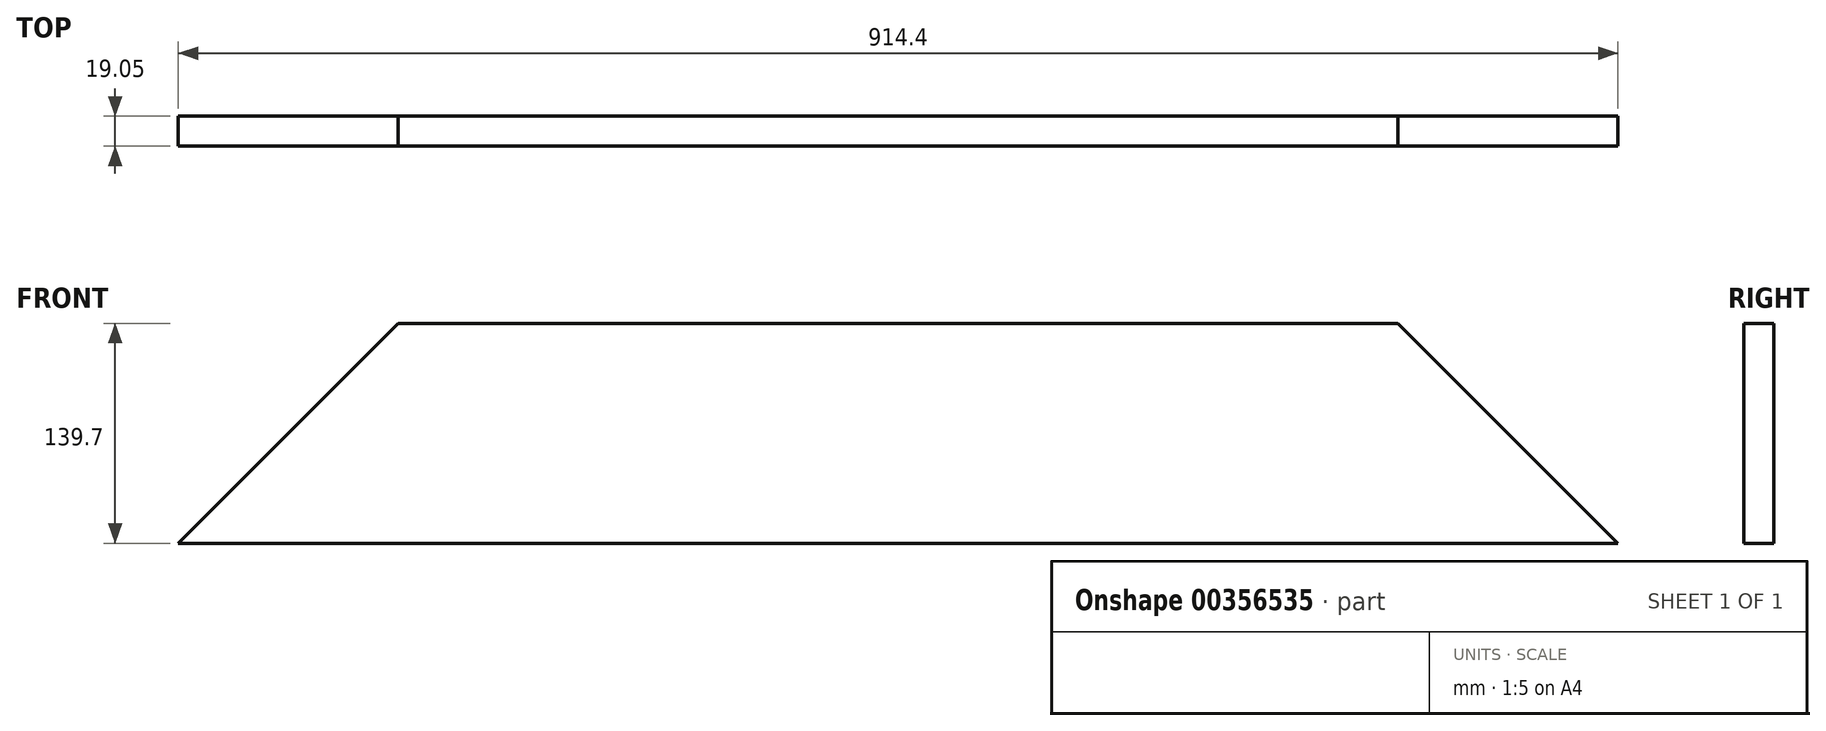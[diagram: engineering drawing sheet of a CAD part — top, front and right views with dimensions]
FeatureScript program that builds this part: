
annotation { "Feature Type Name" : "Feature", "Feature Type Description" : "" }
export const myFeature = defineFeature(function(context is Context, id is Id, definition is map)
    precondition{}
    {
        {
            var Q0;
            Q0=qCreatedBy(makeId("Front.planeOp"),FACE);
            var sketch = newSketch(context, id + "F0", { "sketchPlane" : qUnion([Q0])});
            skLineSegment(sketch, "E0", {"start": v(0, 0) * mm, "end": v(914.4, 0) * mm});
            skLineSegment(sketch, "E1", {"start": v(914.4, 0) * mm, "end": v(774.7, 139.7) * mm});
            skLineSegment(sketch, "E2", {"start": v(774.7, 139.7) * mm, "end": v(139.7, 139.7) * mm});
            skLineSegment(sketch, "E3", {"start": v(139.7, 139.7) * mm, "end": v(0, 0) * mm});
            skSolve(sketch);
        }
        {
            var Q0;
            Q0 = qSketchRegion(id + "F0", true);
            extrude(context, id + "F1", {"entities" : qUnion([Q0]), "oppositeDirection" : true, "depth" : 19.05 * mm});
        }
    });
